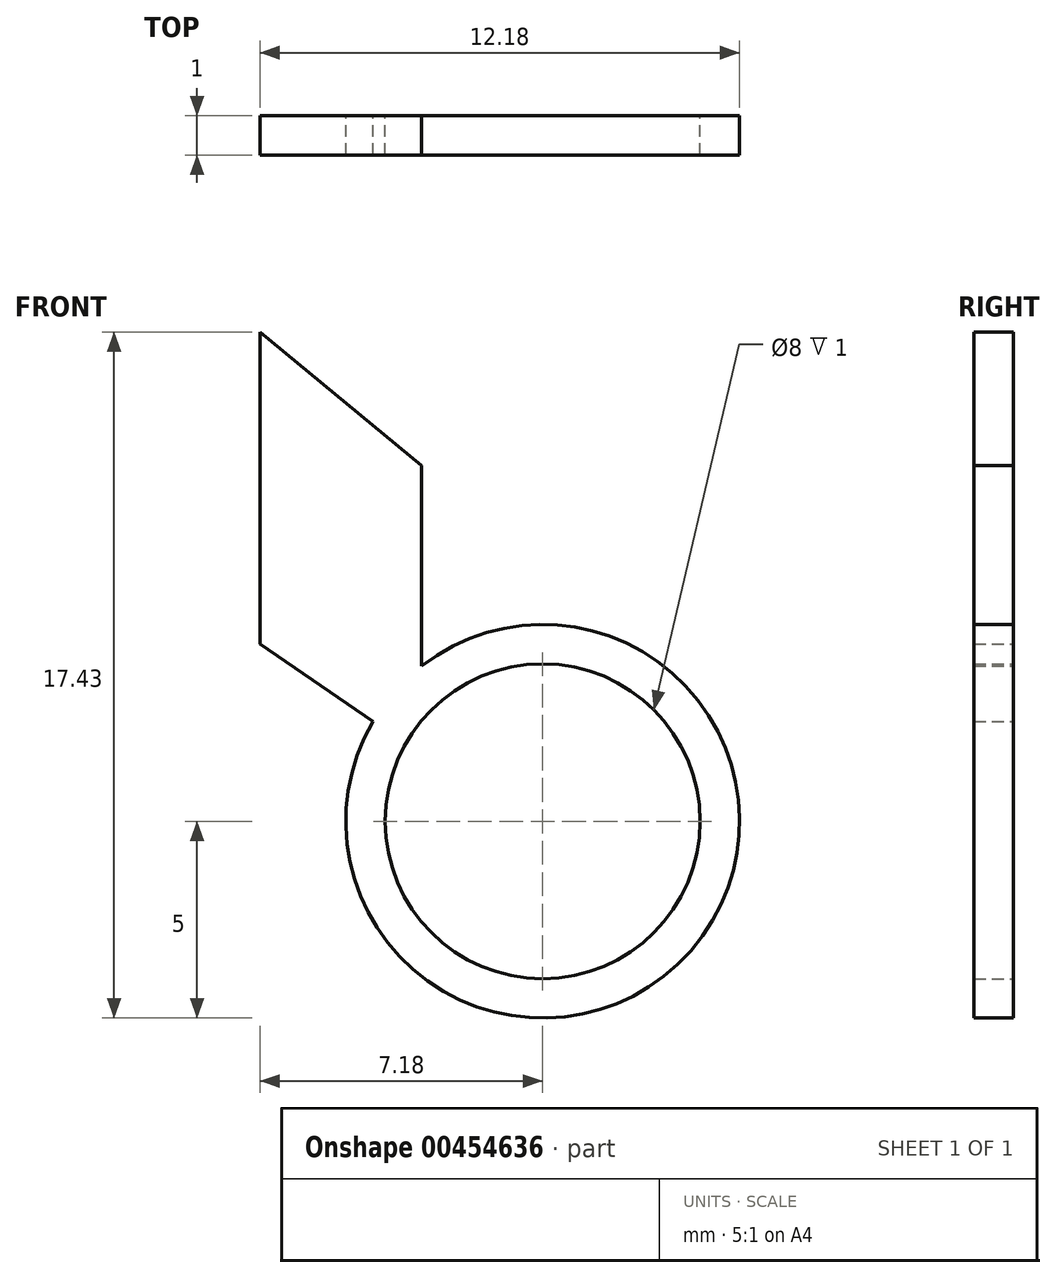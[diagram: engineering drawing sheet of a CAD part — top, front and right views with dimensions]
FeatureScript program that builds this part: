
annotation { "Feature Type Name" : "Feature", "Feature Type Description" : "" }
export const myFeature = defineFeature(function(context is Context, id is Id, definition is map)
    precondition{}
    {
        {
            var Q0;
            Q0=qCreatedBy(makeId("Front.planeOp"),FACE);
            var sketch = newSketch(context, id + "F0", { "sketchPlane" : qUnion([Q0])});
            skArc(sketch, "E0", {"start": v(-4.31, 2.53) * mm, "mid": v(3.76, -3.3) * mm, "end": v(-3.08, 3.94) * mm});
            skCircle(sketch, "E1", {"center": v(0, 0) * mm, "radius": 4 * mm});
            skLineSegment(sketch, "E2", {"start": v(-4.31, 2.53) * mm, "end": v(-7.18, 4.5) * mm});
            skLineSegment(sketch, "E3", {"start": v(-7.18, 4.5) * mm, "end": v(-7.18, 12.43) * mm});
            skLineSegment(sketch, "E4", {"start": v(-7.18, 12.43) * mm, "end": v(-3.08, 9.04) * mm});
            skLineSegment(sketch, "E5", {"start": v(-3.08, 9.04) * mm, "end": v(-3.08, 3.94) * mm});
            skSolve(sketch);
        }
        {
            var Q0;
            Q0 = qSketchRegion(id + "F0", true);
            extrude(context, id + "F1", {"entities" : qUnion([Q0]), "depth" : 1 * mm});
        }
    });
